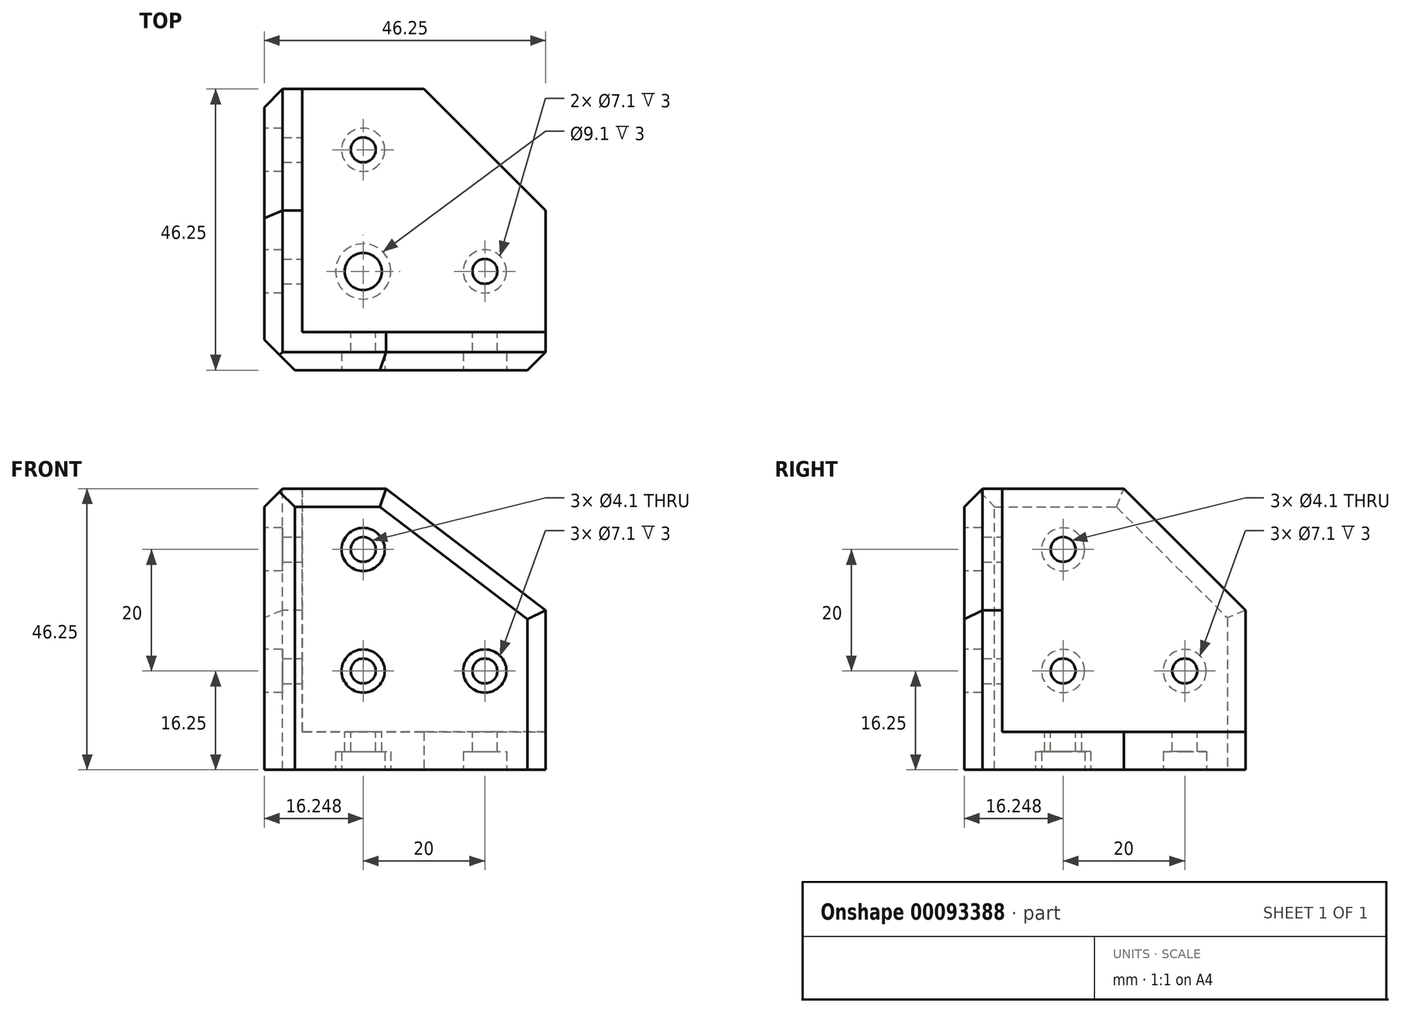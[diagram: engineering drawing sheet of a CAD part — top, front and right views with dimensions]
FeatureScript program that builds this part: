
annotation { "Feature Type Name" : "Feature", "Feature Type Description" : "" }
export const myFeature = defineFeature(function(context is Context, id is Id, definition is map)
    precondition{}
    {
        {
            var Q0;
            Q0=qCreatedBy(makeId("Top.planeOp"),FACE);
            var sketch = newSketch(context, id + "F0", { "sketchPlane" : qUnion([Q0])});
            skLineSegment(sketch, "E0", {"start": v(-22.1, 32.56) * mm, "end": v(-22.1, -13.7) * mm});
            skLineSegment(sketch, "E1", {"start": v(-22.1, -13.7) * mm, "end": v(24.15, -13.7) * mm});
            skLineSegment(sketch, "E2", {"start": v(24.15, -13.7) * mm, "end": v(24.15, 12.56) * mm});
            skLineSegment(sketch, "E3", {"start": v(24.15, 12.56) * mm, "end": v(4.15, 32.56) * mm});
            skLineSegment(sketch, "E4", {"start": v(4.15, 32.56) * mm, "end": v(-22.1, 32.56) * mm});
            skLineSegment(sketch, "E5", {"start": v(-15.85, 32.56) * mm, "end": v(-15.85, -7.44) * mm, "construction": true});
            skLineSegment(sketch, "E6", {"start": v(-15.85, -7.44) * mm, "end": v(24.15, -7.44) * mm, "construction": true});
            skSolve(sketch);
        }
        {
            var Q0;
            Q0 = qSketchRegion(id + "F0", true);
            extrude(context, id + "F1", {"entities" : qUnion([Q0]), "depth" : 6.25 * mm});
        }
        {
            var Q0;
            Q0=makeQuery(id+"F1.opExtrude","SWEPT_FACE",FACE,{"disambiguationData":[OSD([sQuery(id+"F0.wireOp",EDGE,"E1")])]});
            var sketch = newSketch(context, id + "F2", { "sketchPlane" : qUnion([Q0])});
            skLineSegment(sketch, "E7", {"start": v(-22.1, 6.25) * mm, "end": v(24.15, 6.25) * mm});
            skLineSegment(sketch, "E8", {"start": v(24.15, 6.25) * mm, "end": v(24.15, 26.25) * mm});
            skLineSegment(sketch, "E9", {"start": v(24.15, 26.25) * mm, "end": v(-2.1, 46.25) * mm});
            skLineSegment(sketch, "E10", {"start": v(-22.1, 6.25) * mm, "end": v(-22.1, 46.25) * mm});
            skLineSegment(sketch, "E11", {"start": v(-22.1, 46.25) * mm, "end": v(-2.1, 46.25) * mm});
            skSolve(sketch);
        }
        {
            var Q0;
            Q0 = qSketchRegion(id + "F2", true);
            extrude(context, id + "F3", {"entities" : qUnion([Q0]), "oppositeDirection" : true, "depth" : 6.25 * mm});
        }
        {
            var Q0;
            Q0=makeQuery(id+"F3.opExtrude","SWEPT_FACE",FACE,{"disambiguationData":[OSD([sQuery(id+"F2.wireOp",EDGE,"E10")])]});
            var sketch = newSketch(context, id + "F4", { "sketchPlane" : qUnion([Q0])});
            skLineSegment(sketch, "E12", {"start": v(7.44, 6.25) * mm, "end": v(-32.56, 6.25) * mm});
            skLineSegment(sketch, "E13", {"start": v(7.44, 6.25) * mm, "end": v(7.44, 46.25) * mm});
            skLineSegment(sketch, "E14", {"start": v(7.44, 46.25) * mm, "end": v(-12.56, 46.25) * mm});
            skLineSegment(sketch, "E15", {"start": v(-12.56, 46.25) * mm, "end": v(-32.56, 26.25) * mm});
            skLineSegment(sketch, "E16", {"start": v(-32.56, 26.25) * mm, "end": v(-32.56, 6.25) * mm});
            skSolve(sketch);
        }
        {
            var Q0;
            Q0 = qSketchRegion(id + "F4", true);
            extrude(context, id + "F5", {"entities" : qUnion([Q0]), "oppositeDirection" : true, "depth" : 6.25 * mm});
        }
        {
            var Q0;
            Q0=makeQuery(id+"F1.opExtrude","CAP_FACE",FACE,{"disambiguationData":[OSD([sQuery(id+"F0.wireOp",EDGE,"E0"),sQuery(id+"F0.wireOp",EDGE,"E1"),sQuery(id+"F0.wireOp",EDGE,"E2"),sQuery(id+"F0.wireOp",EDGE,"E3"),sQuery(id+"F0.wireOp",EDGE,"E4")])],"isStart":false});
            var sketch = newSketch(context, id + "F6", { "sketchPlane" : qUnion([Q0])});
            skCircle(sketch, "E17", {"center": v(-5.85, 22.56) * mm, "radius": 2.05 * mm});
            skCircle(sketch, "E18", {"center": v(-5.85, 2.56) * mm, "radius": 3.05 * mm});
            skCircle(sketch, "E19", {"center": v(14.15, 2.56) * mm, "radius": 2.05 * mm});
            skSolve(sketch);
        }
        {
            var Q0;
            Q0 = qSketchRegion(id + "F6", true);
            extrude(context, id + "F7", {"entities" : qUnion([Q0]), "operationType" : NewBodyOperationType.REMOVE, "oppositeDirection" : true, "depth" : 25 * mm});
        }
        {
            var Q0;
            Q0=makeQuery(id+"F3.opExtrude","CAP_FACE",FACE,{"disambiguationData":[OSD([sQuery(id+"F2.wireOp",EDGE,"E7"),sQuery(id+"F2.wireOp",EDGE,"E8"),sQuery(id+"F2.wireOp",EDGE,"E9"),sQuery(id+"F2.wireOp",EDGE,"E10"),sQuery(id+"F2.wireOp",EDGE,"E11")])],"isStart":false});
            var sketch = newSketch(context, id + "F8", { "sketchPlane" : qUnion([Q0])});
            skCircle(sketch, "E20", {"center": v(5.85, 16.25) * mm, "radius": 2.05 * mm});
            skCircle(sketch, "E21", {"center": v(-14.15, 16.25) * mm, "radius": 2.05 * mm});
            skCircle(sketch, "E22", {"center": v(5.85, 36.25) * mm, "radius": 2.05 * mm});
            skSolve(sketch);
        }
        {
            var Q0;
            Q0 = qSketchRegion(id + "F8", true);
            extrude(context, id + "F9", {"entities" : qUnion([Q0]), "operationType" : NewBodyOperationType.REMOVE, "oppositeDirection" : true, "depth" : 25 * mm});
        }
        {
            var Q0;
            Q0=makeQuery(id+"F5.opExtrude","CAP_FACE",FACE,{"disambiguationData":[OSD([sQuery(id+"F4.wireOp",EDGE,"E12"),sQuery(id+"F4.wireOp",EDGE,"E13"),sQuery(id+"F4.wireOp",EDGE,"E14"),sQuery(id+"F4.wireOp",EDGE,"E15"),sQuery(id+"F4.wireOp",EDGE,"E16")])],"isStart":false});
            var sketch = newSketch(context, id + "F10", { "sketchPlane" : qUnion([Q0])});
            skCircle(sketch, "E23", {"center": v(22.56, 16.25) * mm, "radius": 2.05 * mm});
            skCircle(sketch, "E24", {"center": v(2.56, 16.25) * mm, "radius": 2.05 * mm});
            skCircle(sketch, "E25", {"center": v(2.56, 36.25) * mm, "radius": 2.05 * mm});
            skSolve(sketch);
        }
        {
            var Q0;
            Q0 = qSketchRegion(id + "F10", true);
            extrude(context, id + "F11", {"entities" : qUnion([Q0]), "operationType" : NewBodyOperationType.REMOVE, "oppositeDirection" : true, "depth" : 25 * mm});
        }
        {
            var Q0;
            Q0=makeQuery(id+"F1.opExtrude","SWEPT_BODY",BODY,{"disambiguationData":[OSD([sQuery(id+"F0.wireOp",EDGE,"E0"),sQuery(id+"F0.wireOp",EDGE,"E1"),sQuery(id+"F0.wireOp",EDGE,"E2"),sQuery(id+"F0.wireOp",EDGE,"E3"),sQuery(id+"F0.wireOp",EDGE,"E4")])]});
            var Q1;
            Q1=makeQuery(id+"F3.opExtrude","SWEPT_BODY",BODY,{"disambiguationData":[OSD([sQuery(id+"F2.wireOp",EDGE,"E7"),sQuery(id+"F2.wireOp",EDGE,"E8"),sQuery(id+"F2.wireOp",EDGE,"E9"),sQuery(id+"F2.wireOp",EDGE,"E10"),sQuery(id+"F2.wireOp",EDGE,"E11")])]});
            var Q2;
            Q2=makeQuery(id+"F5.opExtrude","SWEPT_BODY",BODY,{"disambiguationData":[OSD([sQuery(id+"F4.wireOp",EDGE,"E12"),sQuery(id+"F4.wireOp",EDGE,"E13"),sQuery(id+"F4.wireOp",EDGE,"E14"),sQuery(id+"F4.wireOp",EDGE,"E15"),sQuery(id+"F4.wireOp",EDGE,"E16")])]});
            booleanBodies(context, id + "F12", {"operationType" : BooleanOperationType.UNION, "tools" : qUnion([Q0, Q1, Q2])});
        }
        {
            var Q0;
            Q0=makeQuery(id+"F12.opBoolean","MERGE",FACE,{"derivedFrom":[makeQuery(id+"F1.opExtrude","SWEPT_FACE",FACE,{"disambiguationData":[OSD([sQuery(id+"F0.wireOp",EDGE,"E1")])]}),makeQuery(id+"F3.opExtrude","CAP_FACE",FACE,{"disambiguationData":[OSD([sQuery(id+"F2.wireOp",EDGE,"E7"),sQuery(id+"F2.wireOp",EDGE,"E8"),sQuery(id+"F2.wireOp",EDGE,"E9"),sQuery(id+"F2.wireOp",EDGE,"E10"),sQuery(id+"F2.wireOp",EDGE,"E11")])],"isStart":true})]});
            var sketch = newSketch(context, id + "F13", { "sketchPlane" : qUnion([Q0])});
            skCircle(sketch, "E26", {"center": v(-5.85, 36.25) * mm, "radius": 3.55 * mm});
            skCircle(sketch, "E27", {"center": v(14.15, 16.25) * mm, "radius": 3.55 * mm});
            skCircle(sketch, "E28", {"center": v(-5.85, 16.25) * mm, "radius": 3.55 * mm});
            skSolve(sketch);
        }
        {
            var Q0;
            Q0 = qSketchRegion(id + "F13", true);
            extrude(context, id + "F14", {"entities" : qUnion([Q0]), "operationType" : NewBodyOperationType.REMOVE, "oppositeDirection" : true, "depth" : 3 * mm});
        }
        {
            var Q0;
            Q0=makeQuery(id+"F12.opBoolean","MERGE",FACE,{"derivedFrom":[makeQuery(id+"F1.opExtrude","SWEPT_FACE",FACE,{"disambiguationData":[OSD([sQuery(id+"F0.wireOp",EDGE,"E0")])]}),makeQuery(id+"F3.opExtrude","SWEPT_FACE",FACE,{"disambiguationData":[OSD([sQuery(id+"F2.wireOp",EDGE,"E10")])]}),makeQuery(id+"F5.opExtrude","CAP_FACE",FACE,{"disambiguationData":[OSD([sQuery(id+"F4.wireOp",EDGE,"E12"),sQuery(id+"F4.wireOp",EDGE,"E13"),sQuery(id+"F4.wireOp",EDGE,"E14"),sQuery(id+"F4.wireOp",EDGE,"E15"),sQuery(id+"F4.wireOp",EDGE,"E16")])],"isStart":true})]});
            var sketch = newSketch(context, id + "F15", { "sketchPlane" : qUnion([Q0])});
            skCircle(sketch, "E29", {"center": v(-2.56, 36.25) * mm, "radius": 3.55 * mm});
            skCircle(sketch, "E30", {"center": v(-2.56, 16.25) * mm, "radius": 3.55 * mm});
            skCircle(sketch, "E31", {"center": v(-22.56, 16.25) * mm, "radius": 3.55 * mm});
            skSolve(sketch);
        }
        {
            var Q0;
            Q0 = qSketchRegion(id + "F15", true);
            extrude(context, id + "F16", {"entities" : qUnion([Q0]), "operationType" : NewBodyOperationType.REMOVE, "oppositeDirection" : true, "depth" : 3 * mm});
        }
        {
            var Q0;
            Q0=makeQuery(id+"F1.opExtrude","CAP_FACE",FACE,{"disambiguationData":[OSD([sQuery(id+"F0.wireOp",EDGE,"E0"),sQuery(id+"F0.wireOp",EDGE,"E1"),sQuery(id+"F0.wireOp",EDGE,"E2"),sQuery(id+"F0.wireOp",EDGE,"E3"),sQuery(id+"F0.wireOp",EDGE,"E4")])],"isStart":true});
            var sketch = newSketch(context, id + "F17", { "sketchPlane" : qUnion([Q0])});
            skCircle(sketch, "E32", {"center": v(-5.85, -22.56) * mm, "radius": 3.55 * mm});
            skCircle(sketch, "E33", {"center": v(-5.85, -2.56) * mm, "radius": 4.55 * mm});
            skCircle(sketch, "E34", {"center": v(14.15, -2.56) * mm, "radius": 3.55 * mm});
            skSolve(sketch);
        }
        {
            var Q0;
            Q0 = qSketchRegion(id + "F17", true);
            extrude(context, id + "F18", {"entities" : qUnion([Q0]), "operationType" : NewBodyOperationType.REMOVE, "oppositeDirection" : true, "depth" : 3 * mm});
        }
        {
            var Q0;
            Q0=makeQuery(id+"F12.opBoolean","MERGE",EDGE,{"derivedFrom":[makeQuery(id+"F1.opExtrude","SWEPT_EDGE",EDGE,{"disambiguationData":[OSD([sQuery(id+"F0.wireOp",EDGE,"E0"),sQuery(id+"F0.wireOp",EDGE,"E1")])]}),makeQuery(id+"F3.opExtrude","CAP_EDGE",EDGE,{"disambiguationData":[OSD([sQuery(id+"F2.wireOp",EDGE,"E10")])],"isStart":true})]});
            chamfer(context, id + "F19", {"entities" : qUnion([Q0]), "width" : 5 * mm, "tangentPropagation" : true});
        }
        {
            var Q0;
            Q0=makeQuery(id+"F3.opExtrude","CAP_EDGE",EDGE,{"disambiguationData":[OSD([sQuery(id+"F2.wireOp",EDGE,"E11")])],"isStart":true});
            var Q1;
            Q1=makeQuery(id+"F12.opBoolean","MERGE",EDGE,{"derivedFrom":[makeQuery(id+"F3.opExtrude","SWEPT_EDGE",EDGE,{"disambiguationData":[OSD([sQuery(id+"F2.wireOp",EDGE,"E10"),sQuery(id+"F2.wireOp",EDGE,"E11")])]}),makeQuery(id+"F5.opExtrude","CAP_EDGE",EDGE,{"disambiguationData":[OSD([sQuery(id+"F4.wireOp",EDGE,"E14")])],"isStart":true})]});
            var Q2;
            Q2=makeQuery(id+"F3.opExtrude","CAP_EDGE",EDGE,{"disambiguationData":[OSD([sQuery(id+"F2.wireOp",EDGE,"E9")])],"isStart":true});
            var Q3;
            Q3=makeQuery(id+"F5.opExtrude","CAP_EDGE",EDGE,{"disambiguationData":[OSD([sQuery(id+"F4.wireOp",EDGE,"E15")])],"isStart":true});
            var Q4;
            Q4=makeQuery(id+"F12.opBoolean","MERGE",EDGE,{"derivedFrom":[makeQuery(id+"F1.opExtrude","SWEPT_EDGE",EDGE,{"disambiguationData":[OSD([sQuery(id+"F0.wireOp",EDGE,"E1"),sQuery(id+"F0.wireOp",EDGE,"E2")])]}),makeQuery(id+"F3.opExtrude","CAP_EDGE",EDGE,{"disambiguationData":[OSD([sQuery(id+"F2.wireOp",EDGE,"E8")])],"isStart":true})]});
            var Q5;
            Q5=makeQuery(id+"F12.opBoolean","MERGE",EDGE,{"derivedFrom":[makeQuery(id+"F1.opExtrude","SWEPT_EDGE",EDGE,{"disambiguationData":[OSD([sQuery(id+"F0.wireOp",EDGE,"E0"),sQuery(id+"F0.wireOp",EDGE,"E4")])]}),makeQuery(id+"F5.opExtrude","CAP_EDGE",EDGE,{"disambiguationData":[OSD([sQuery(id+"F4.wireOp",EDGE,"E16")])],"isStart":true})]});
            chamfer(context, id + "F20", {"entities" : qUnion([Q0, Q1, Q2, Q3, Q4, Q5]), "width" : 3 * mm, "tangentPropagation" : true});
        }
    });
